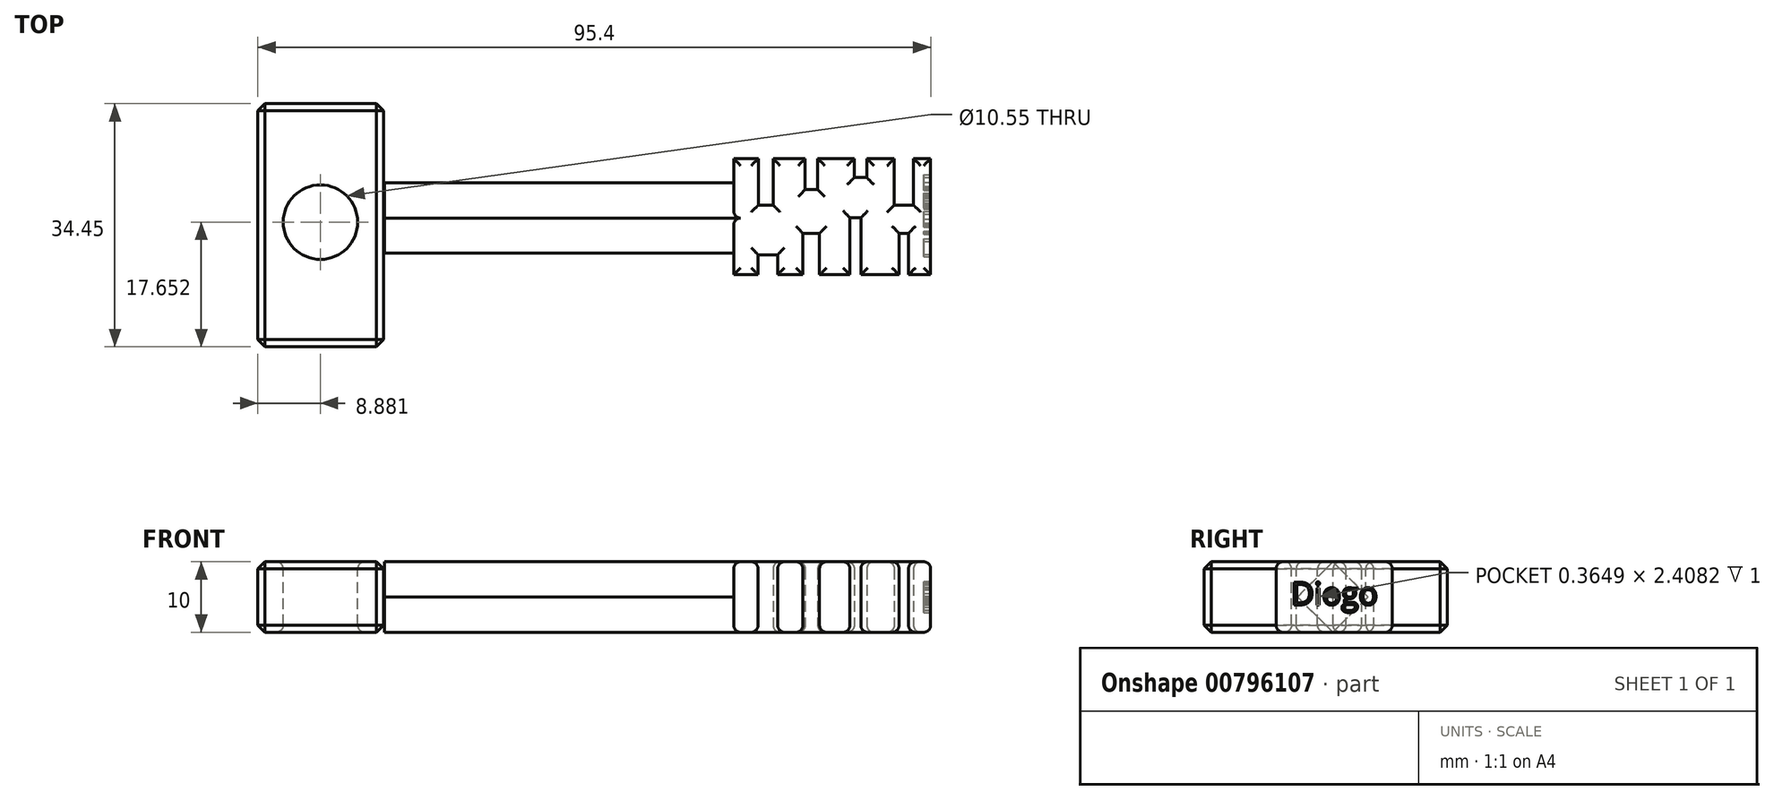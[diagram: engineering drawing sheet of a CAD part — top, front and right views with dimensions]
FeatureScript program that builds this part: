
annotation { "Feature Type Name" : "Feature", "Feature Type Description" : "" }
export const myFeature = defineFeature(function(context is Context, id is Id, definition is map)
    precondition{}
    {
        {
            var Q0;
            Q0=qCreatedBy(makeId("Top.planeOp"),FACE);
            var sketch = newSketch(context, id + "F0", { "sketchPlane" : qUnion([Q0])});
            skLineSegment(sketch, "E0.bottom", {"start": v(-20.1, 23.24) * mm, "end": v(29.9, 23.24) * mm});
            skLineSegment(sketch, "E0.top", {"start": v(-20.1, 13.24) * mm, "end": v(29.9, 13.24) * mm});
            skLineSegment(sketch, "E0.left", {"start": v(-20.1, 23.24) * mm, "end": v(-20.1, 13.24) * mm});
            skLineSegment(sketch, "E0.right", {"start": v(29.9, 23.24) * mm, "end": v(29.9, 13.24) * mm});
            skSolve(sketch);
        }
        {
            var Q0;
            Q0 = qSketchRegion(id + "F0", true);
            extrude(context, id + "F1", {"entities" : qUnion([Q0]), "depth" : 10 * mm, "offsetDistance" : 25 * mm});
        }
        {
            var Q0;
            Q0=qCreatedBy(makeId("Top.planeOp"),FACE);
            var sketch = newSketch(context, id + "F2", { "sketchPlane" : qUnion([Q0])});
            skLineSegment(sketch, "E1.bottom", {"start": v(-38.05, 34.45) * mm, "end": v(-20.2, 34.45) * mm});
            skLineSegment(sketch, "E1.top", {"start": v(-38.05, 0) * mm, "end": v(-20.2, 0) * mm});
            skLineSegment(sketch, "E1.left", {"start": v(-38.05, 34.45) * mm, "end": v(-38.05, 0) * mm});
            skLineSegment(sketch, "E1.right", {"start": v(-20.2, 34.45) * mm, "end": v(-20.2, 0) * mm});
            skSolve(sketch);
        }
        {
            var Q0;
            Q0 = qSketchRegion(id + "F2", true);
            extrude(context, id + "F3", {"entities" : qUnion([Q0]), "depth" : 10 * mm, "offsetDistance" : 25 * mm});
        }
        {
            var Q0;
            Q0=makeQuery(id+"F3.opExtrude","CAP_FACE",FACE,{"disambiguationData":[OSD([sQuery(id+"F2.wireOp",EDGE,"E1.bottom"),sQuery(id+"F2.wireOp",EDGE,"E1.top"),sQuery(id+"F2.wireOp",EDGE,"E1.left"),sQuery(id+"F2.wireOp",EDGE,"E1.right")])],"isStart":false});
            var sketch = newSketch(context, id + "F4", { "sketchPlane" : qUnion([Q0])});
            skCircle(sketch, "E2", {"center": v(-29.17, 17.65) * mm, "radius": 5.28 * mm});
            skSolve(sketch);
        }
        {
            var Q0;
            Q0 = qSketchRegion(id + "F4", true);
            extrude(context, id + "F5", {"entities" : qUnion([Q0]), "operationType" : NewBodyOperationType.REMOVE, "oppositeDirection" : true, "depth" : 15 * mm, "offsetDistance" : 25 * mm});
        }
        {
            var Q0;
            Q0=makeQuery(id+"F3.opExtrude","CAP_EDGE",EDGE,{"disambiguationData":[OSD([sQuery(id+"F2.wireOp",EDGE,"E1.right")])],"isStart":false});
            var Q1;
            Q1=makeQuery(id+"F3.opExtrude","CAP_EDGE",EDGE,{"disambiguationData":[OSD([sQuery(id+"F2.wireOp",EDGE,"E1.top")])],"isStart":false});
            var Q2;
            Q2=makeQuery(id+"F3.opExtrude","CAP_EDGE",EDGE,{"disambiguationData":[OSD([sQuery(id+"F2.wireOp",EDGE,"E1.left")])],"isStart":false});
            var Q3;
            Q3=makeQuery(id+"F3.opExtrude","CAP_EDGE",EDGE,{"disambiguationData":[OSD([sQuery(id+"F2.wireOp",EDGE,"E1.bottom")])],"isStart":false});
            var Q4;
            Q4=makeQuery(id+"F3.opExtrude","SWEPT_EDGE",EDGE,{"disambiguationData":[OSD([sQuery(id+"F2.wireOp",EDGE,"E1.bottom"),sQuery(id+"F2.wireOp",EDGE,"E1.left")])]});
            var Q5;
            Q5=makeQuery(id+"F3.opExtrude","SWEPT_EDGE",EDGE,{"disambiguationData":[OSD([sQuery(id+"F2.wireOp",EDGE,"E1.top"),sQuery(id+"F2.wireOp",EDGE,"E1.left")])]});
            var Q6;
            Q6=makeQuery(id+"F3.opExtrude","SWEPT_EDGE",EDGE,{"disambiguationData":[OSD([sQuery(id+"F2.wireOp",EDGE,"E1.top"),sQuery(id+"F2.wireOp",EDGE,"E1.right")])]});
            var Q7;
            Q7=makeQuery(id+"F3.opExtrude","SWEPT_EDGE",EDGE,{"disambiguationData":[OSD([sQuery(id+"F2.wireOp",EDGE,"E1.bottom"),sQuery(id+"F2.wireOp",EDGE,"E1.right")])]});
            var Q8;
            Q8=makeQuery(id+"F3.opExtrude","CAP_EDGE",EDGE,{"disambiguationData":[OSD([sQuery(id+"F2.wireOp",EDGE,"E1.left")])],"isStart":true});
            var Q9;
            Q9=makeQuery(id+"F3.opExtrude","CAP_EDGE",EDGE,{"disambiguationData":[OSD([sQuery(id+"F2.wireOp",EDGE,"E1.bottom")])],"isStart":true});
            var Q10;
            Q10=makeQuery(id+"F3.opExtrude","CAP_EDGE",EDGE,{"disambiguationData":[OSD([sQuery(id+"F2.wireOp",EDGE,"E1.top")])],"isStart":true});
            var Q11;
            Q11=makeQuery(id+"F3.opExtrude","CAP_EDGE",EDGE,{"disambiguationData":[OSD([sQuery(id+"F2.wireOp",EDGE,"E1.right")])],"isStart":true});
            chamfer(context, id + "F6", {"entities" : qUnion([Q0, Q1, Q2, Q3, Q4, Q5, Q6, Q7, Q8, Q9, Q10, Q11]), "width" : 1 * mm, "tangentPropagation" : true});
        }
        {
            var Q0;
            Q0=qCreatedBy(makeId("Top.planeOp"),FACE);
            var sketch = newSketch(context, id + "F7", { "sketchPlane" : qUnion([Q0])});
            skLineSegment(sketch, "E3.bottom", {"start": v(29.42, 26.67) * mm, "end": v(57.35, 26.67) * mm});
            skLineSegment(sketch, "E3.top", {"start": v(29.42, 10.19) * mm, "end": v(57.35, 10.19) * mm});
            skLineSegment(sketch, "E3.left", {"start": v(29.42, 26.67) * mm, "end": v(29.42, 10.19) * mm});
            skLineSegment(sketch, "E3.right", {"start": v(57.35, 26.67) * mm, "end": v(57.35, 10.19) * mm});
            skSolve(sketch);
        }
        {
            var Q0;
            Q0 = qSketchRegion(id + "F7", true);
            extrude(context, id + "F8", {"entities" : qUnion([Q0]), "operationType" : NewBodyOperationType.ADD, "depth" : 10 * mm, "offsetDistance" : 25 * mm});
        }
        {
            var Q0;
            Q0=makeQuery(id+"F8.opExtrude","CAP_FACE",FACE,{"disambiguationData":[OSD([sQuery(id+"F7.wireOp",EDGE,"E3.bottom"),sQuery(id+"F7.wireOp",EDGE,"E3.top"),sQuery(id+"F7.wireOp",EDGE,"E3.left"),sQuery(id+"F7.wireOp",EDGE,"E3.right")])],"isStart":false});
            var sketch = newSketch(context, id + "F9", { "sketchPlane" : qUnion([Q0])});
            skLineSegment(sketch, "E4.bottom", {"start": v(32.89, 10.19) * mm, "end": v(35.64, 10.19) * mm});
            skLineSegment(sketch, "E4.top", {"start": v(32.89, 13.04) * mm, "end": v(35.64, 13.04) * mm});
            skLineSegment(sketch, "E4.left", {"start": v(32.89, 10.19) * mm, "end": v(32.89, 13.04) * mm});
            skLineSegment(sketch, "E4.right", {"start": v(35.64, 10.19) * mm, "end": v(35.64, 13.04) * mm});
            skLineSegment(sketch, "E5.bottom", {"start": v(39.24, 10.19) * mm, "end": v(41.6, 10.19) * mm});
            skLineSegment(sketch, "E5.top", {"start": v(39.24, 16.07) * mm, "end": v(41.6, 16.07) * mm});
            skLineSegment(sketch, "E5.left", {"start": v(39.24, 10.19) * mm, "end": v(39.24, 16.07) * mm});
            skLineSegment(sketch, "E5.right", {"start": v(41.6, 10.19) * mm, "end": v(41.6, 16.07) * mm});
            skLineSegment(sketch, "E6.bottom", {"start": v(45.9, 10.19) * mm, "end": v(47.44, 10.19) * mm});
            skLineSegment(sketch, "E6.top", {"start": v(45.9, 18.28) * mm, "end": v(47.44, 18.28) * mm});
            skLineSegment(sketch, "E6.left", {"start": v(45.9, 10.19) * mm, "end": v(45.9, 18.28) * mm});
            skLineSegment(sketch, "E6.right", {"start": v(47.44, 10.19) * mm, "end": v(47.44, 18.28) * mm});
            skLineSegment(sketch, "E7.bottom", {"start": v(52.87, 10.19) * mm, "end": v(54.2, 10.19) * mm});
            skLineSegment(sketch, "E7.top", {"start": v(52.87, 16.07) * mm, "end": v(54.2, 16.07) * mm});
            skLineSegment(sketch, "E7.left", {"start": v(52.87, 10.19) * mm, "end": v(52.87, 16.07) * mm});
            skLineSegment(sketch, "E7.right", {"start": v(54.2, 10.19) * mm, "end": v(54.2, 16.07) * mm});
            skSolve(sketch);
        }
        {
            var Q0;
            Q0 = qSketchRegion(id + "F9", true);
            extrude(context, id + "F10", {"entities" : qUnion([Q0]), "operationType" : NewBodyOperationType.REMOVE, "oppositeDirection" : true, "depth" : 25 * mm, "offsetDistance" : 25 * mm});
        }
        {
            var Q0;
            Q0=makeQuery(id+"F8.opExtrude","CAP_FACE",FACE,{"disambiguationData":[OSD([sQuery(id+"F7.wireOp",EDGE,"E3.bottom"),sQuery(id+"F7.wireOp",EDGE,"E3.top"),sQuery(id+"F7.wireOp",EDGE,"E3.left"),sQuery(id+"F7.wireOp",EDGE,"E3.right")])],"isStart":true});
            var sketch = newSketch(context, id + "F11", { "sketchPlane" : qUnion([Q0])});
            skLineSegment(sketch, "E8.bottom", {"start": v(32.92, -26.67) * mm, "end": v(35, -26.67) * mm});
            skLineSegment(sketch, "E8.top", {"start": v(32.92, -20.07) * mm, "end": v(35, -20.07) * mm});
            skLineSegment(sketch, "E8.left", {"start": v(32.92, -26.67) * mm, "end": v(32.92, -20.07) * mm});
            skLineSegment(sketch, "E8.right", {"start": v(35, -26.67) * mm, "end": v(35, -20.07) * mm});
            skLineSegment(sketch, "E9.bottom", {"start": v(39.56, -26.67) * mm, "end": v(41.32, -26.67) * mm});
            skLineSegment(sketch, "E9.top", {"start": v(39.56, -22.28) * mm, "end": v(41.32, -22.28) * mm});
            skLineSegment(sketch, "E9.left", {"start": v(39.56, -26.67) * mm, "end": v(39.56, -22.28) * mm});
            skLineSegment(sketch, "E9.right", {"start": v(41.32, -26.67) * mm, "end": v(41.32, -22.28) * mm});
            skLineSegment(sketch, "E10.bottom", {"start": v(46.52, -26.67) * mm, "end": v(48.3, -26.67) * mm});
            skLineSegment(sketch, "E10.top", {"start": v(46.52, -23.98) * mm, "end": v(48.3, -23.98) * mm});
            skLineSegment(sketch, "E10.left", {"start": v(46.52, -26.67) * mm, "end": v(46.52, -23.98) * mm});
            skLineSegment(sketch, "E10.right", {"start": v(48.3, -26.67) * mm, "end": v(48.3, -23.98) * mm});
            skLineSegment(sketch, "E11.bottom", {"start": v(52.19, -26.67) * mm, "end": v(54.92, -26.67) * mm});
            skLineSegment(sketch, "E11.top", {"start": v(52.19, -20.07) * mm, "end": v(54.92, -20.07) * mm});
            skLineSegment(sketch, "E11.left", {"start": v(52.19, -26.67) * mm, "end": v(52.19, -20.07) * mm});
            skLineSegment(sketch, "E11.right", {"start": v(54.92, -26.67) * mm, "end": v(54.92, -20.07) * mm});
            skSolve(sketch);
        }
        {
            var Q0;
            Q0 = qSketchRegion(id + "F11", true);
            extrude(context, id + "F12", {"entities" : qUnion([Q0]), "operationType" : NewBodyOperationType.REMOVE, "oppositeDirection" : true, "depth" : 25 * mm, "offsetDistance" : 25 * mm});
        }
        {
            var Q0;
            Q0=makeQuery(id+"F5.boolean.opBoolean","INTERSECT",EDGE,{"derivedFrom":[makeQuery(id+"F3.opExtrude","CAP_FACE",FACE,{"disambiguationData":[OSD([sQuery(id+"F2.wireOp",EDGE,"E1.bottom"),sQuery(id+"F2.wireOp",EDGE,"E1.top"),sQuery(id+"F2.wireOp",EDGE,"E1.left"),sQuery(id+"F2.wireOp",EDGE,"E1.right")])],"isStart":true}),makeQuery(id+"F5.opExtrude","SWEPT_FACE",FACE,{"disambiguationData":[OSD([sQuery(id+"F4.wireOp",EDGE,"E2")])]})]});
            var Q1;
            Q1=makeQuery(id+"F5.boolean.opBoolean","COPY",EDGE,{"derivedFrom":makeQuery(id+"F5.opExtrude","CAP_EDGE",EDGE,{"disambiguationData":[OSD([sQuery(id+"F4.wireOp",EDGE,"E2")])],"isStart":true})});
            var Q2;
            Q2=makeQuery(id+"F5.boolean.opBoolean","COPY",FACE,{"derivedFrom":makeQuery(id+"F5.opExtrude","SWEPT_FACE",FACE,{"disambiguationData":[OSD([sQuery(id+"F4.wireOp",EDGE,"E2")])]})});
            fillet(context, id + "F13", {"entities" : qUnion([Q0, Q1, Q2]), "radius" : 1 * mm, "tangentPropagation" : true, "allowEdgeOverflow" : false});
        }
        {
            var Q0;
            Q0=makeQuery(id+"F1.opExtrude","CAP_EDGE",EDGE,{"disambiguationData":[OSD([sQuery(id+"F0.wireOp",EDGE,"E0.bottom")])],"isStart":true});
            var Q1;
            Q1=makeQuery(id+"F1.opExtrude","CAP_EDGE",EDGE,{"disambiguationData":[OSD([sQuery(id+"F0.wireOp",EDGE,"E0.top")])],"isStart":true});
            var Q2;
            Q2=makeQuery(id+"F1.opExtrude","CAP_EDGE",EDGE,{"disambiguationData":[OSD([sQuery(id+"F0.wireOp",EDGE,"E0.top")])],"isStart":false});
            var Q3;
            Q3=makeQuery(id+"F1.opExtrude","CAP_EDGE",EDGE,{"disambiguationData":[OSD([sQuery(id+"F0.wireOp",EDGE,"E0.bottom")])],"isStart":false});
            chamfer(context, id + "F14", {"entities" : qUnion([Q0, Q1, Q2, Q3]), "width" : 5 * mm, "tangentPropagation" : true});
        }
        {
            var Q0;
            {var subQ0=sQuery(id+"F7.wireOp",EDGE,"E3.top");var subQ1=sQuery(id+"F7.wireOp",EDGE,"E3.right");Q0=makeQuery(id+"F10.boolean.opBoolean","SPLIT",EDGE,{"disambiguationData":[TD([makeQuery(id+"F8.opExtrude","SWEPT_FACE",FACE,{"disambiguationData":[OSD([subQ1])]})])],"derivedFrom":makeQuery(id+"F8.opExtrude","CAP_EDGE",EDGE,{"disambiguationData":[OSD([subQ0])],"isStart":false})});}
            var Q1;
            {var subQ0=sQuery(id+"F7.wireOp",EDGE,"E3.top");Q1=makeQuery(id+"F10.boolean.opBoolean","SPLIT",EDGE,{"disambiguationData":[TD([makeQuery(id+"F10.opExtrude","SWEPT_FACE",FACE,{"disambiguationData":[OSD([sQuery(id+"F9.wireOp",EDGE,"E6.right")])]})])],"derivedFrom":makeQuery(id+"F8.opExtrude","CAP_EDGE",EDGE,{"disambiguationData":[OSD([subQ0])],"isStart":false})});}
            var Q2;
            {var subQ0=sQuery(id+"F7.wireOp",EDGE,"E3.top");Q2=makeQuery(id+"F10.boolean.opBoolean","SPLIT",EDGE,{"disambiguationData":[TD([makeQuery(id+"F10.opExtrude","SWEPT_FACE",FACE,{"disambiguationData":[OSD([sQuery(id+"F9.wireOp",EDGE,"E5.right")])]})])],"derivedFrom":makeQuery(id+"F8.opExtrude","CAP_EDGE",EDGE,{"disambiguationData":[OSD([subQ0])],"isStart":false})});}
            var Q3;
            {var subQ0=sQuery(id+"F7.wireOp",EDGE,"E3.top");Q3=makeQuery(id+"F10.boolean.opBoolean","SPLIT",EDGE,{"disambiguationData":[TD([makeQuery(id+"F10.opExtrude","SWEPT_FACE",FACE,{"disambiguationData":[OSD([sQuery(id+"F9.wireOp",EDGE,"E4.right")])]})])],"derivedFrom":makeQuery(id+"F8.opExtrude","CAP_EDGE",EDGE,{"disambiguationData":[OSD([subQ0])],"isStart":false})});}
            var Q4;
            Q4=makeQuery(id+"F10.boolean.opBoolean","COPY",EDGE,{"derivedFrom":makeQuery(id+"F10.opExtrude","CAP_EDGE",EDGE,{"disambiguationData":[OSD([sQuery(id+"F9.wireOp",EDGE,"E4.top")])],"isStart":true})});
            var Q5;
            {var subQ0=sQuery(id+"F7.wireOp",EDGE,"E3.left");var subQ1=sQuery(id+"F7.wireOp",EDGE,"E3.top");Q5=makeQuery(id+"F10.boolean.opBoolean","SPLIT",EDGE,{"disambiguationData":[TD([makeQuery(id+"F8.opExtrude","SWEPT_FACE",FACE,{"disambiguationData":[OSD([subQ0])]})])],"derivedFrom":makeQuery(id+"F8.opExtrude","CAP_EDGE",EDGE,{"disambiguationData":[OSD([subQ1])],"isStart":false})});}
            var Q6;
            Q6=makeQuery(id+"F10.boolean.opBoolean","COPY",EDGE,{"derivedFrom":makeQuery(id+"F10.opExtrude","CAP_EDGE",EDGE,{"disambiguationData":[OSD([sQuery(id+"F9.wireOp",EDGE,"E4.left")])],"isStart":true})});
            var Q7;
            Q7=makeQuery(id+"F10.boolean.opBoolean","COPY",EDGE,{"derivedFrom":makeQuery(id+"F10.opExtrude","CAP_EDGE",EDGE,{"disambiguationData":[OSD([sQuery(id+"F9.wireOp",EDGE,"E5.left")])],"isStart":true})});
            var Q8;
            Q8=makeQuery(id+"F10.boolean.opBoolean","COPY",EDGE,{"derivedFrom":makeQuery(id+"F10.opExtrude","CAP_EDGE",EDGE,{"disambiguationData":[OSD([sQuery(id+"F9.wireOp",EDGE,"E5.top")])],"isStart":true})});
            var Q9;
            Q9=makeQuery(id+"F10.boolean.opBoolean","COPY",EDGE,{"derivedFrom":makeQuery(id+"F10.opExtrude","CAP_EDGE",EDGE,{"disambiguationData":[OSD([sQuery(id+"F9.wireOp",EDGE,"E5.right")])],"isStart":true})});
            var Q10;
            Q10=makeQuery(id+"F10.boolean.opBoolean","COPY",EDGE,{"derivedFrom":makeQuery(id+"F10.opExtrude","CAP_EDGE",EDGE,{"disambiguationData":[OSD([sQuery(id+"F9.wireOp",EDGE,"E4.right")])],"isStart":true})});
            var Q11;
            Q11=makeQuery(id+"F10.boolean.opBoolean","COPY",EDGE,{"derivedFrom":makeQuery(id+"F10.opExtrude","CAP_EDGE",EDGE,{"disambiguationData":[OSD([sQuery(id+"F9.wireOp",EDGE,"E6.right")])],"isStart":true})});
            var Q12;
            Q12=makeQuery(id+"F8.boolean.opBoolean","MERGE",FACE,{"derivedFrom":[makeQuery(id+"F1.opExtrude","CAP_FACE",FACE,{"disambiguationData":[OSD([sQuery(id+"F0.wireOp",EDGE,"E0.bottom"),sQuery(id+"F0.wireOp",EDGE,"E0.top"),sQuery(id+"F0.wireOp",EDGE,"E0.left"),sQuery(id+"F0.wireOp",EDGE,"E0.right")])],"isStart":false}),makeQuery(id+"F8.opExtrude","CAP_FACE",FACE,{"disambiguationData":[OSD([sQuery(id+"F7.wireOp",EDGE,"E3.bottom"),sQuery(id+"F7.wireOp",EDGE,"E3.top"),sQuery(id+"F7.wireOp",EDGE,"E3.left"),sQuery(id+"F7.wireOp",EDGE,"E3.right")])],"isStart":false})]});
            var Q13;
            Q13=makeQuery(id+"F8.boolean.opBoolean","MERGE",FACE,{"derivedFrom":[makeQuery(id+"F1.opExtrude","CAP_FACE",FACE,{"disambiguationData":[OSD([sQuery(id+"F0.wireOp",EDGE,"E0.bottom"),sQuery(id+"F0.wireOp",EDGE,"E0.top"),sQuery(id+"F0.wireOp",EDGE,"E0.left"),sQuery(id+"F0.wireOp",EDGE,"E0.right")])],"isStart":true}),makeQuery(id+"F8.opExtrude","CAP_FACE",FACE,{"disambiguationData":[OSD([sQuery(id+"F7.wireOp",EDGE,"E3.bottom"),sQuery(id+"F7.wireOp",EDGE,"E3.top"),sQuery(id+"F7.wireOp",EDGE,"E3.left"),sQuery(id+"F7.wireOp",EDGE,"E3.right")])],"isStart":true})]});
            fillet(context, id + "F15", {"entities" : qUnion([Q0, Q1, Q2, Q3, Q4, Q5, Q6, Q7, Q8, Q9, Q10, Q11, Q12, Q13]), "radius" : 1 * mm, "tangentPropagation" : true, "allowEdgeOverflow" : false});
        }
        {
            var Q0;
            Q0=makeQuery(id+"F8.opExtrude","SWEPT_FACE",FACE,{"disambiguationData":[OSD([sQuery(id+"F7.wireOp",EDGE,"E3.right")])]});
            var sketch = newSketch(context, id + "F16", { "sketchPlane" : qUnion([Q0])});
            skText(sketch, "E12", { "text": "Diogo\n", "fontName": "OpenSans-Regular.ttf"});
            const initialGuessF16  = {"E12": [0.01229, 0.00387, 1, 0, 0.00324]};
            skSetInitialGuess(sketch, initialGuessF16);
            skSolve(sketch);
        }
        {
            var Q0;
            Q0 = qSketchRegion(id + "F16", true);
            extrude(context, id + "F17", {"entities" : qUnion([Q0]), "operationType" : NewBodyOperationType.REMOVE, "oppositeDirection" : true, "depth" : 1 * mm, "offsetDistance" : 25 * mm});
        }
    });
